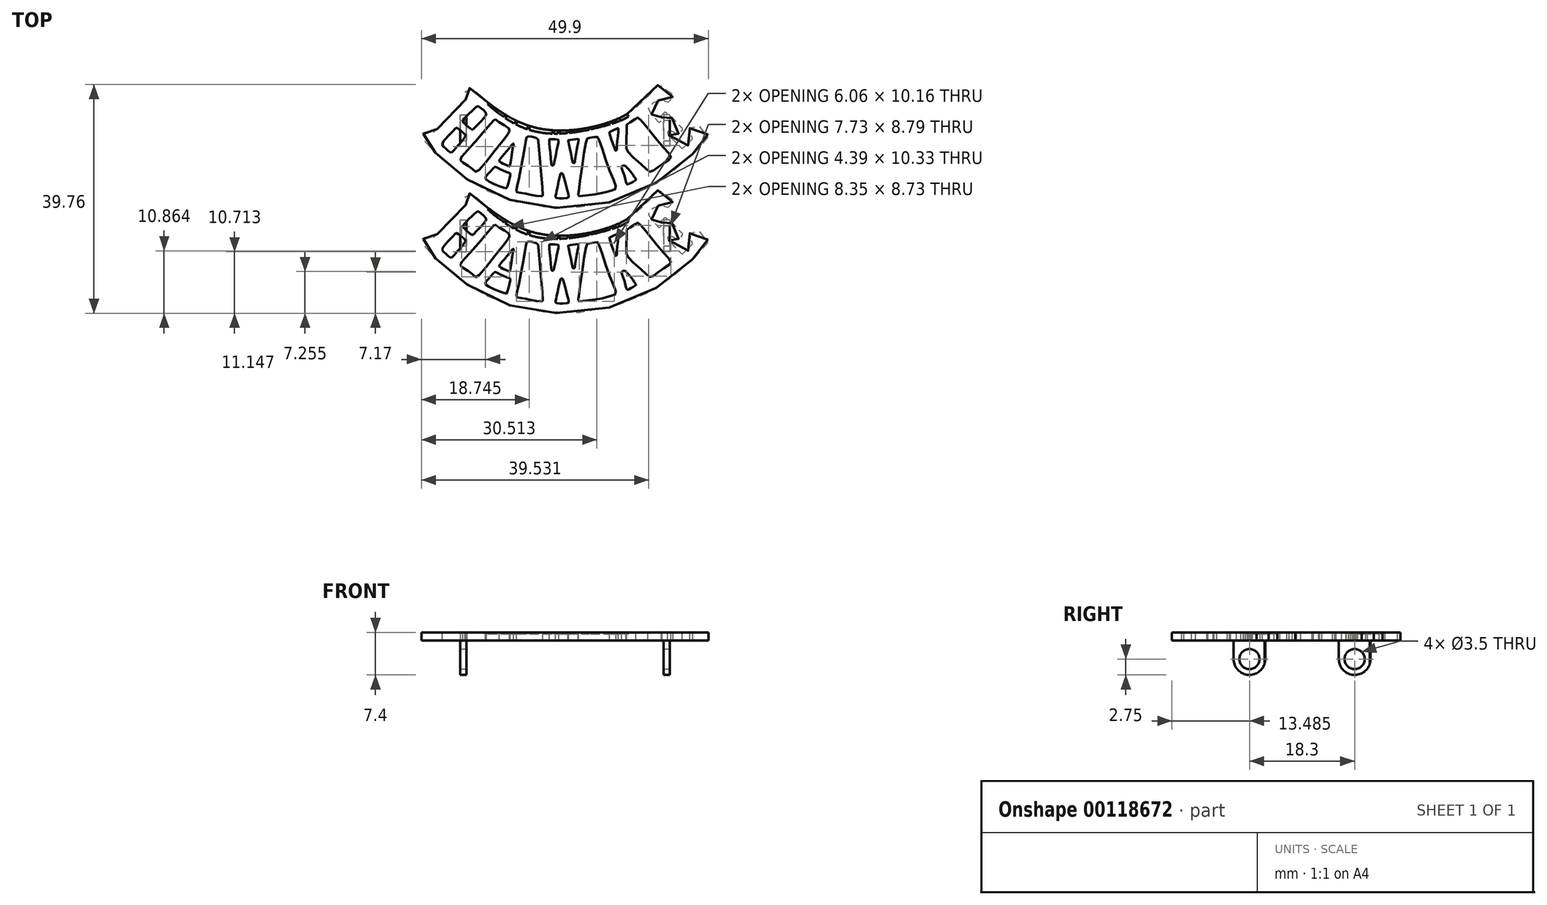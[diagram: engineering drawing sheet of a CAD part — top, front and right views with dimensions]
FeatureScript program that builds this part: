
annotation { "Feature Type Name" : "Feature", "Feature Type Description" : "" }
export const myFeature = defineFeature(function(context is Context, id is Id, definition is map)
    precondition{}
    {
        {
            var Q0;
            Q0=qCreatedBy(makeId("Top.planeOp"),FACE);
            var sketch = newSketch(context, id + "F0", { "sketchPlane" : qUnion([Q0])});
            skLineSegment(sketch, "E0.bottom", {"start": v(-25, 25) * mm, "end": v(25, 25) * mm, "construction": true});
            skLineSegment(sketch, "E0.top", {"start": v(-25, -25) * mm, "end": v(25, -25) * mm, "construction": true});
            skLineSegment(sketch, "E0.left", {"start": v(-25, 25) * mm, "end": v(-25, -25) * mm, "construction": true});
            skLineSegment(sketch, "E0.right", {"start": v(25, 25) * mm, "end": v(25, -25) * mm, "construction": true});
            skPoint(sketch, "E0.middle", {"position": v(0, 0) * mm});
            skFitSpline(sketch, "E1", {"points": [v(-16.8, 10.33) * mm, v(-16.35, 10.54) * mm, v(-16.05, 10.38) * mm, v(-14.88, 9.2) * mm, v(-8.76, 4.94) * mm, v(-1.08, 3.08) * mm, v(7.1, 4.34) * mm, v(12.96, 7.57) * mm, v(16.13, 10.99) * mm, v(16.21, 11.07) * mm, v(16.51, 10.96) * mm, v(18.78, 9.3) * mm, v(18.8, 9.14) * mm, v(18.17, 8.01) * mm, v(18.09, 7.96) * mm, v(17.29, 8.23) * mm, v(16.27, 8.34) * mm, v(14.83, 7.46) * mm, v(14.45, 6.77) * mm, v(14.56, 6.5) * mm, v(16.27, 4.54) * mm, v(16.43, 4.4) * mm, v(16.82, 4.73) * mm, v(16.87, 5.12) * mm, v(16.76, 5.72) * mm, v(16.98, 6.03) * mm, v(17.62, 6.41) * mm, v(17.81, 6.25) * mm, v(20.02, 3.85) * mm, v(20.37, 3.55) * mm, v(20.37, 3.24) * mm, v(19.66, 2.47) * mm, v(19.4, 2.47) * mm, v(18.58, 2.94) * mm, v(17.92, 2.86) * mm, v(17.84, 2.7) * mm, v(19.96, -0.01) * mm, v(20.2, -0.15) * mm, v(21.31, 0.43) * mm, v(22.2, 1.73) * mm, v(21.95, 3.02) * mm, v(21.73, 3.43) * mm, v(21.73, 3.57) * mm, v(22.7, 4.31) * mm, v(22.82, 4.31) * mm, v(24.88, 2.33) * mm, v(24.92, 2.16) * mm, v(24.78, 1.83) * mm, v(22.72, -0.54) * mm, v(18.13, -4.47) * mm, v(12.27, -7.86) * mm, v(4.07, -10.1) * mm, v(-3.83, -10.19) * mm, v(-9.9, -8.88) * mm, v(-15.88, -6.15) * mm, v(-20.81, -2.4) * mm, v(-23.4, 0.07) * mm, v(-24.87, 1.83) * mm, v(-24.93, 2.19) * mm, v(-23.94, 3.2) * mm, v(-23.72, 3.24) * mm, v(-23.04, 2.76) * mm, v(-22.86, 2.76) * mm, v(-19, 6.6) * mm, v(-17.17, 8.55) * mm, v(-17.03, 8.82) * mm, v(-17.33, 9.62) * mm, v(-17.37, 9.78) * mm, v(-16.8, 10.33) * mm]});
            skFitSpline(sketch, "E2", {"points": [v(-16.68, 6) * mm, v(-15.57, 7.06) * mm, v(-15.24, 7.28) * mm, v(-14.93, 7.23) * mm, v(-13.75, 6.16) * mm, v(-13.7, 5.9) * mm, v(-13.9, 5.53) * mm, v(-16, 3.28) * mm, v(-16.24, 3.26) * mm, v(-17.73, 4.61) * mm, v(-17.76, 4.78) * mm, v(-17.65, 5) * mm, v(-16.68, 6) * mm]});
            skFitSpline(sketch, "E3", {"points": [v(-20.35, 2.1) * mm, v(-19.34, 3.16) * mm, v(-19, 3.52) * mm, v(-18.71, 3.52) * mm, v(-17.8, 2.75) * mm, v(-17.31, 2.32) * mm, v(-17.48, 1.83) * mm, v(-18.84, 0.23) * mm, v(-19.6, -0.61) * mm, v(-20.02, -0.71) * mm, v(-20.68, -0.08) * mm, v(-21.3, 0.47) * mm, v(-21.32, 0.86) * mm, v(-20.93, 1.47) * mm, v(-20.35, 2.1) * mm]});
            skFitSpline(sketch, "E4", {"points": [v(-15.5, 1.26) * mm, v(-13.73, 3.35) * mm, v(-12.52, 4.73) * mm, v(-12.26, 4.97) * mm, v(-12.03, 4.97) * mm, v(-11.45, 4.49) * mm, v(-9.9, 3.58) * mm, v(-9.66, 3.22) * mm, v(-9.68, 2.82) * mm, v(-11, 1.11) * mm, v(-15.2, -4.01) * mm, v(-15.59, -4.08) * mm, v(-16.2, -3.51) * mm, v(-17.4, -2.7) * mm, v(-18.1, -2.16) * mm, v(-18.16, -1.8) * mm, v(-17.52, -0.95) * mm, v(-15.5, 1.26) * mm]});
            skFitSpline(sketch, "E5", {"points": [v(-9.17, 0.7) * mm, v(-10.6, -1.03) * mm, v(-11.39, -2) * mm, v(-11.44, -2.23) * mm, v(-10.8, -2.67) * mm, v(-9.64, -3.14) * mm, v(-9.58, -3.08) * mm, v(-8.98, 0.65) * mm, v(-8.98, 0.79) * mm, v(-9.07, 0.82) * mm, v(-9.17, 0.7) * mm]});
            skFitSpline(sketch, "E6", {"points": [v(-9.72, -4.26) * mm, v(-11.01, -3.78) * mm, v(-11.97, -3.26) * mm, v(-12.14, -3.2) * mm, v(-12.44, -3.43) * mm, v(-13.75, -4.9) * mm, v(-13.84, -5.15) * mm, v(-13.66, -5.52) * mm, v(-10.5, -6.91) * mm, v(-10.19, -6.91) * mm, v(-9.63, -5.15) * mm, v(-9.56, -4.37) * mm, v(-9.72, -4.26) * mm]});
            skFitSpline(sketch, "E7", {"points": [v(-6.8, 1.44) * mm, v(-7.66, -3.4) * mm, v(-8.38, -6.96) * mm, v(-8.47, -7.39) * mm, v(-8.4, -7.62) * mm, v(-7.21, -7.83) * mm, v(-6.26, -8.05) * mm, v(-4.53, -8.3) * mm, v(-3.88, -8.28) * mm, v(-3.84, -8.12) * mm, v(-4.62, 1.33) * mm, v(-4.67, 1.53) * mm, v(-4.86, 1.7) * mm, v(-5.45, 1.95) * mm, v(-6.28, 2.07) * mm, v(-6.59, 2.04) * mm, v(-6.72, 1.86) * mm, v(-6.8, 1.44) * mm]});
            skFitSpline(sketch, "E8", {"points": [v(-2.74, 1.4) * mm, v(-2.37, -2.7) * mm, v(-2.28, -3) * mm, v(-2.09, -2.96) * mm, v(-1.86, -2.38) * mm, v(-1.13, 1.18) * mm, v(-1.1, 1.34) * mm, v(-1.14, 1.46) * mm, v(-2.47, 1.58) * mm, v(-2.71, 1.55) * mm, v(-2.74, 1.4) * mm]});
            skFitSpline(sketch, "E9", {"points": [v(-0.83, -4.61) * mm, v(-1.37, -7.05) * mm, v(-1.61, -8.24) * mm, v(-1.61, -8.52) * mm, v(-1.1, -8.7) * mm, v(0.5, -8.6) * mm, v(0.63, -8.47) * mm, v(0.46, -7.55) * mm, v(-0.22, -5) * mm, v(-0.36, -4.54) * mm, v(-0.54, -4.3) * mm, v(-0.73, -4.41) * mm, v(-0.83, -4.61) * mm]});
            skFitSpline(sketch, "E10", {"points": [v(1.29, -2.14) * mm, v(0.68, 0.68) * mm, v(0.56, 1.17) * mm, v(0.56, 1.36) * mm, v(1.58, 1.57) * mm, v(2.32, 1.6) * mm, v(2.37, 1.4) * mm, v(2.1, 0.14) * mm, v(1.67, -2.45) * mm, v(1.6, -2.6) * mm, v(1.42, -2.54) * mm, v(1.29, -2.14) * mm]});
            skFitSpline(sketch, "E11", {"points": [v(2.51, -8.3) * mm, v(5.22, -8.01) * mm, v(7.06, -7.63) * mm, v(7.76, -7.4) * mm, v(8.66, -7.17) * mm, v(8.89, -6.8) * mm, v(8.15, -4.84) * mm, v(6.27, 0.5) * mm, v(5.7, 1.95) * mm, v(5.57, 2.01) * mm, v(4.71, 1.85) * mm, v(4.1, 1.79) * mm, v(3.9, 1.69) * mm, v(3.47, 0.18) * mm, v(2.41, -7.2) * mm, v(2.32, -8.05) * mm, v(2.38, -8.26) * mm, v(2.51, -8.3) * mm]});
            skFitSpline(sketch, "E12", {"points": [v(7.76, 2.6) * mm, v(8.68, -0.22) * mm, v(8.75, -0.38) * mm, v(8.92, -0.38) * mm, v(9, -0.1) * mm, v(9.3, 3.3) * mm, v(9.3, 3.43) * mm, v(9.26, 3.5) * mm, v(8.96, 3.37) * mm, v(7.81, 2.82) * mm, v(7.74, 2.76) * mm, v(7.76, 2.6) * mm]});
            skFitSpline(sketch, "E13", {"points": [v(10.62, -5.84) * mm, v(10, -3.8) * mm, v(9.89, -3.15) * mm, v(10.27, -3) * mm, v(10.62, -3.18) * mm, v(11.84, -4.65) * mm, v(12.34, -5.41) * mm, v(12.31, -5.5) * mm, v(11.62, -5.94) * mm, v(10.98, -6.27) * mm, v(10.86, -6.29) * mm, v(10.7, -6.13) * mm, v(10.62, -5.84) * mm]});
            skFitSpline(sketch, "E14", {"points": [v(15.97, 1.48) * mm, v(14.22, 3.68) * mm, v(12.96, 5.15) * mm, v(12.72, 5.33) * mm, v(12.5, 5.3) * mm, v(12.07, 5) * mm, v(11.03, 4.33) * mm, v(10.77, 4.13) * mm, v(10.74, 3.56) * mm, v(10.63, 0.28) * mm, v(10.74, -0.33) * mm, v(11.56, -1.27) * mm, v(13.9, -3.38) * mm, v(14.58, -4.03) * mm, v(15.04, -4.07) * mm, v(15.58, -3.75) * mm, v(16.46, -3.05) * mm, v(17.98, -2.05) * mm, v(18.33, -1.78) * mm, v(18.42, -1.4) * mm, v(17.88, -0.67) * mm, v(15.97, 1.48) * mm]});
            skSolve(sketch);
        }
        {
            var Q0;
            Q0=makeQuery(id+"F0.imprint","IMPRINT",FACE,{"disambiguationData":[TD([[makeQuery(id+"F0.imprint","IMPRINT",EDGE,{"derivedFrom":sQuery(id+"F0.wireOp",EDGE,"E1")}),-1.0]])]});
            extrude(context, id + "F1", {"entities" : qUnion([Q0]), "oppositeDirection" : true, "depth" : 1.4 * mm, "offsetDistance" : 25 * mm});
        }
        {
            var Q0;
            Q0=makeQuery(id+"F1.opExtrude","CAP_FACE",FACE,{"disambiguationData":[OSD([sQuery(id+"F0.wireOp",EDGE,"E1"),sQuery(id+"F0.wireOp",EDGE,"E2"),sQuery(id+"F0.wireOp",EDGE,"E3"),sQuery(id+"F0.wireOp",EDGE,"E4"),sQuery(id+"F0.wireOp",EDGE,"E5"),sQuery(id+"F0.wireOp",EDGE,"E6"),sQuery(id+"F0.wireOp",EDGE,"E7"),sQuery(id+"F0.wireOp",EDGE,"E8"),sQuery(id+"F0.wireOp",EDGE,"E9"),sQuery(id+"F0.wireOp",EDGE,"E10"),sQuery(id+"F0.wireOp",EDGE,"E11"),sQuery(id+"F0.wireOp",EDGE,"E12"),sQuery(id+"F0.wireOp",EDGE,"E13"),sQuery(id+"F0.wireOp",EDGE,"E14")])],"isStart":true});
            var sketch = newSketch(context, id + "F2", { "sketchPlane" : qUnion([Q0])});
            skFitSpline(sketch, "E15.0.0", {"points": [v(-16.8, 10.33) * mm, v(-17.02, 10.15) * mm, v(-17.45, 9.79) * mm, v(-17.32, 9.63) * mm, v(-16.93, 8.79) * mm, v(-17.24, 8.49) * mm, v(-18.92, 6.66) * mm, v(-22.8, 2.67) * mm, v(-23.03, 2.73) * mm, v(-23.74, 3.3) * mm, v(-23.94, 3.24) * mm, v(-25.09, 2.2) * mm, v(-24.87, 1.77) * mm, v(-23.26, -0.17) * mm, v(-20.78, -2.48) * mm, v(-15.96, -6.48) * mm, v(-9.93, -9.08) * mm, v(-3.8, -10.44) * mm, v(4.14, -10.5) * mm, v(12.37, -8.2) * mm, v(18.13, -4.69) * mm, v(22.52, -0.88) * mm, v(24.8, 1.68) * mm, v(24.92, 2.16) * mm, v(24.98, 2.36) * mm, v(22.8, 4.38) * mm, v(22.74, 4.33) * mm, v(21.63, 3.6) * mm, v(21.73, 3.42) * mm, v(22, 3) * mm, v(22.44, 1.63) * mm, v(21.46, 0.38) * mm, v(20.17, -0.22) * mm, v(19.98, -0.06) * mm, v(17.62, 2.67) * mm, v(17.93, 2.88) * mm, v(18.62, 3.1) * mm, v(19.4, 2.43) * mm, v(19.67, 2.4) * mm, v(20.47, 3.2) * mm, v(20.4, 3.6) * mm, v(19.97, 3.77) * mm, v(17.78, 6.2) * mm, v(17.66, 6.51) * mm, v(16.95, 6.02) * mm, v(16.68, 5.76) * mm, v(16.9, 5.1) * mm, v(16.9, 4.73) * mm, v(16.4, 4.32) * mm, v(16.29, 4.58) * mm, v(14.5, 6.5) * mm, v(14.4, 6.76) * mm, v(14.77, 7.59) * mm, v(16.26, 8.53) * mm, v(17.2, 8.28) * mm, v(18.1, 7.92) * mm, v(18.17, 8) * mm, v(18.84, 9.17) * mm, v(18.85, 9.31) * mm, v(16.56, 11.01) * mm, v(16.2, 11.1) * mm, v(16.08, 10.92) * mm, v(12.74, 6.78) * mm, v(7.26, 4) * mm, v(-1.2, 2.55) * mm, v(-8.68, 4.24) * mm, v(-14.76, 8.91) * mm, v(-15.97, 10.34) * mm, v(-16.36, 10.62) * mm, v(-16.61, 10.46) * mm, v(-16.8, 10.33) * mm]});
            skLineSegment(sketch, "E16", {"start": v(-13.15, 8.37) * mm, "end": v(-15.03, 6.44) * mm});
            skLineSegment(sketch, "E17.0", {"start": v(-13.04, 8.06) * mm, "end": v(-14.91, 6.13) * mm});
            skLineSegment(sketch, "E18", {"start": v(-22.3, -1.53) * mm, "end": v(-20.26, 0.58) * mm});
            skLineSegment(sketch, "E19.0", {"start": v(-22.03, -1.69) * mm, "end": v(-20, 0.42) * mm});
            skLineSegment(sketch, "E20", {"start": v(-9.91, 6.24) * mm, "end": v(-11.97, 3.94) * mm});
            skLineSegment(sketch, "E21.0", {"start": v(-9.69, 6.04) * mm, "end": v(-11.74, 3.74) * mm});
            skLineSegment(sketch, "E22", {"start": v(-19.08, -4.59) * mm, "end": v(-16.6, -1.7) * mm});
            skLineSegment(sketch, "E23.0", {"start": v(-18.85, -4.78) * mm, "end": v(-16.37, -1.89) * mm});
            skLineSegment(sketch, "E24", {"start": v(-18.02, -5.51) * mm, "end": v(-15.7, -2.48) * mm});
            skLineSegment(sketch, "E25.0", {"start": v(-17.78, -5.7) * mm, "end": v(-15.47, -2.66) * mm});
            skLineSegment(sketch, "E26", {"start": v(-7.68, 5.41) * mm, "end": v(-10, 2.31) * mm});
            skLineSegment(sketch, "E27.0", {"start": v(-7.92, 5.59) * mm, "end": v(-10.23, 2.5) * mm});
            skLineSegment(sketch, "E28", {"start": v(-6.28, 4.78) * mm, "end": v(-6.73, 1.82) * mm});
            skLineSegment(sketch, "E29.0", {"start": v(-5.98, 4.73) * mm, "end": v(-6.43, 1.78) * mm});
            skLineSegment(sketch, "E30", {"start": v(-13.98, -7.8) * mm, "end": v(-12.3, -4.8) * mm});
            skLineSegment(sketch, "E31.0", {"start": v(-13.72, -7.94) * mm, "end": v(-12.03, -4.94) * mm});
            skLineSegment(sketch, "E32", {"start": v(-12.2, -8.68) * mm, "end": v(-11, -5.3) * mm});
            skLineSegment(sketch, "E33.0", {"start": v(-11.91, -8.78) * mm, "end": v(-10.71, -5.4) * mm});
            skLineSegment(sketch, "E34", {"start": v(-7.84, -10.15) * mm, "end": v(-6.91, -6.26) * mm});
            skLineSegment(sketch, "E35.0", {"start": v(-7.54, -10.22) * mm, "end": v(-6.62, -6.33) * mm});
            skLineSegment(sketch, "E36", {"start": v(-3.73, -10.62) * mm, "end": v(-3.9, -7.27) * mm});
            skLineSegment(sketch, "E37.0", {"start": v(-4.03, -10.64) * mm, "end": v(-4.2, -7.29) * mm});
            skLineSegment(sketch, "E38", {"start": v(-2.09, -10.82) * mm, "end": v(-1.62, -8.25) * mm});
            skLineSegment(sketch, "E39.0", {"start": v(-1.8, -10.87) * mm, "end": v(-1.32, -8.3) * mm});
            skLineSegment(sketch, "E40", {"start": v(0.92, -10.9) * mm, "end": v(0.59, -8.56) * mm});
            skLineSegment(sketch, "E41.0", {"start": v(0.62, -10.95) * mm, "end": v(0.3, -8.6) * mm});
            skLineSegment(sketch, "E42", {"start": v(2.24, -10.74) * mm, "end": v(2.36, -8.22) * mm});
            skLineSegment(sketch, "E43.0", {"start": v(2.54, -10.76) * mm, "end": v(2.66, -8.24) * mm});
            skLineSegment(sketch, "E44", {"start": v(8.3, -9.8) * mm, "end": v(7.53, -6.59) * mm});
            skLineSegment(sketch, "E45.0", {"start": v(8, -9.88) * mm, "end": v(7.24, -6.66) * mm});
            skLineSegment(sketch, "E46", {"start": v(12.01, -8.54) * mm, "end": v(10.87, -5.6) * mm});
            skLineSegment(sketch, "E47.0", {"start": v(12.3, -8.43) * mm, "end": v(11.15, -5.5) * mm});
            skLineSegment(sketch, "E48", {"start": v(13.09, -7.93) * mm, "end": v(11.76, -5.25) * mm});
            skLineSegment(sketch, "E49.0", {"start": v(12.82, -8.06) * mm, "end": v(11.5, -5.38) * mm});
            skLineSegment(sketch, "E50", {"start": v(17.28, -5.7) * mm, "end": v(14.8, -2.5) * mm});
            skLineSegment(sketch, "E51.0", {"start": v(17.52, -5.52) * mm, "end": v(15.04, -2.31) * mm});
            skLineSegment(sketch, "E52", {"start": v(18.7, -4.64) * mm, "end": v(16.52, -1.88) * mm});
            skLineSegment(sketch, "E53.0", {"start": v(18.93, -4.46) * mm, "end": v(16.75, -1.69) * mm});
            skLineSegment(sketch, "E54", {"start": v(-2.14, 4.08) * mm, "end": v(-2.27, 1.13) * mm});
            skLineSegment(sketch, "E55.0", {"start": v(-1.84, 4.1) * mm, "end": v(-1.97, 1.14) * mm});
            skLineSegment(sketch, "E56", {"start": v(-0.77, 4.01) * mm, "end": v(-1.11, 1.32) * mm});
            skLineSegment(sketch, "E57.0", {"start": v(-1.07, 4.05) * mm, "end": v(-1.4, 1.36) * mm});
            skLineSegment(sketch, "E58", {"start": v(0.3, 3.53) * mm, "end": v(0.6, 1.39) * mm});
            skLineSegment(sketch, "E59.0", {"start": v(0.6, 3.57) * mm, "end": v(0.9, 1.43) * mm});
            skLineSegment(sketch, "E60", {"start": v(3.99, 4.37) * mm, "end": v(4.78, 0.95) * mm});
            skLineSegment(sketch, "E61.0", {"start": v(4.28, 4.43) * mm, "end": v(5.07, 1.02) * mm});
            skLineSegment(sketch, "E62", {"start": v(7.4, 5.44) * mm, "end": v(8.53, 2.45) * mm});
            skLineSegment(sketch, "E63.0", {"start": v(7.68, 5.55) * mm, "end": v(8.8, 2.55) * mm});
            skLineSegment(sketch, "E64", {"start": v(10.22, 6.93) * mm, "end": v(11.97, 3.94) * mm});
            skLineSegment(sketch, "E65.0", {"start": v(10.48, 7.08) * mm, "end": v(12.23, 4.09) * mm});
            skSolve(sketch);
        }
        {
            var Q0;
            {var subQ0=sQuery(id+"F2.wireOp",EDGE,"E17.0");var subQ1=sQuery(id+"F2.wireOp",EDGE,"E15.0.0");var subQ2=makeQuery(id+"F2.imprint","INTERSECT",VERTEX,{"derivedFrom":[subQ1,subQ0]});Q0=makeQuery(id+"F2.imprint","IMPRINT",FACE,{"disambiguationData":[TD([[makeQuery(id+"F2.imprint","IMPRINT",EDGE,{"disambiguationData":[TD([[subQ2,1.0]])],"derivedFrom":subQ1}),-1.0]])]});}
            var Q1;
            {var subQ0=sQuery(id+"F2.wireOp",EDGE,"E20");var subQ1=sQuery(id+"F2.wireOp",EDGE,"E15.0.0");var subQ2=makeQuery(id+"F2.imprint","INTERSECT",VERTEX,{"derivedFrom":[subQ1,subQ0]});Q1=makeQuery(id+"F2.imprint","IMPRINT",FACE,{"disambiguationData":[TD([[makeQuery(id+"F2.imprint","IMPRINT",EDGE,{"disambiguationData":[TD([[subQ2,-1.0]])],"derivedFrom":subQ1}),-1.0]])]});}
            var Q2;
            {var subQ0=sQuery(id+"F2.wireOp",EDGE,"E27.0");var subQ1=sQuery(id+"F2.wireOp",EDGE,"E15.0.0");var subQ2=makeQuery(id+"F2.imprint","INTERSECT",VERTEX,{"derivedFrom":[subQ1,subQ0]});Q2=makeQuery(id+"F2.imprint","IMPRINT",FACE,{"disambiguationData":[TD([[makeQuery(id+"F2.imprint","IMPRINT",EDGE,{"disambiguationData":[TD([[subQ2,-1.0]])],"derivedFrom":subQ1}),-1.0]])]});}
            var Q3;
            {var subQ0=sQuery(id+"F2.wireOp",EDGE,"E28");var subQ1=sQuery(id+"F2.wireOp",EDGE,"E15.0.0");var subQ2=makeQuery(id+"F2.imprint","INTERSECT",VERTEX,{"derivedFrom":[subQ1,subQ0]});Q3=makeQuery(id+"F2.imprint","IMPRINT",FACE,{"disambiguationData":[TD([[makeQuery(id+"F2.imprint","IMPRINT",EDGE,{"disambiguationData":[TD([[subQ2,-1.0]])],"derivedFrom":subQ1}),-1.0]])]});}
            var Q4;
            {var subQ0=sQuery(id+"F2.wireOp",EDGE,"E57.0");var subQ1=sQuery(id+"F2.wireOp",EDGE,"E15.0.0");var subQ2=makeQuery(id+"F2.imprint","INTERSECT",VERTEX,{"derivedFrom":[subQ1,subQ0]});Q4=makeQuery(id+"F2.imprint","IMPRINT",FACE,{"disambiguationData":[TD([[makeQuery(id+"F2.imprint","IMPRINT",EDGE,{"disambiguationData":[TD([[subQ2,-1.0]])],"derivedFrom":subQ1}),-1.0]])]});}
            var Q5;
            {var subQ0=sQuery(id+"F2.wireOp",EDGE,"E54");var subQ1=sQuery(id+"F2.wireOp",EDGE,"E15.0.0");var subQ2=makeQuery(id+"F2.imprint","INTERSECT",VERTEX,{"derivedFrom":[subQ1,subQ0]});Q5=makeQuery(id+"F2.imprint","IMPRINT",FACE,{"disambiguationData":[TD([[makeQuery(id+"F2.imprint","IMPRINT",EDGE,{"disambiguationData":[TD([[subQ2,-1.0]])],"derivedFrom":subQ1}),-1.0]])]});}
            var Q6;
            {var subQ0=sQuery(id+"F2.wireOp",EDGE,"E58");var subQ1=sQuery(id+"F2.wireOp",EDGE,"E15.0.0");var subQ2=makeQuery(id+"F2.imprint","INTERSECT",VERTEX,{"derivedFrom":[subQ1,subQ0]});Q6=makeQuery(id+"F2.imprint","IMPRINT",FACE,{"disambiguationData":[TD([[makeQuery(id+"F2.imprint","IMPRINT",EDGE,{"disambiguationData":[TD([[subQ2,-1.0]])],"derivedFrom":subQ1}),-1.0]])]});}
            var Q7;
            {var subQ0=sQuery(id+"F2.wireOp",EDGE,"E60");var subQ1=sQuery(id+"F2.wireOp",EDGE,"E15.0.0");var subQ2=makeQuery(id+"F2.imprint","INTERSECT",VERTEX,{"derivedFrom":[subQ1,subQ0]});Q7=makeQuery(id+"F2.imprint","IMPRINT",FACE,{"disambiguationData":[TD([[makeQuery(id+"F2.imprint","IMPRINT",EDGE,{"disambiguationData":[TD([[subQ2,-1.0]])],"derivedFrom":subQ1}),-1.0]])]});}
            var Q8;
            {var subQ0=sQuery(id+"F2.wireOp",EDGE,"E62");var subQ1=sQuery(id+"F2.wireOp",EDGE,"E15.0.0");var subQ2=makeQuery(id+"F2.imprint","INTERSECT",VERTEX,{"derivedFrom":[subQ1,subQ0]});Q8=makeQuery(id+"F2.imprint","IMPRINT",FACE,{"disambiguationData":[TD([[makeQuery(id+"F2.imprint","IMPRINT",EDGE,{"disambiguationData":[TD([[subQ2,-1.0]])],"derivedFrom":subQ1}),-1.0]])]});}
            var Q9;
            {var subQ0=sQuery(id+"F2.wireOp",EDGE,"E64");var subQ1=sQuery(id+"F2.wireOp",EDGE,"E15.0.0");var subQ2=makeQuery(id+"F2.imprint","INTERSECT",VERTEX,{"derivedFrom":[subQ1,subQ0]});Q9=makeQuery(id+"F2.imprint","IMPRINT",FACE,{"disambiguationData":[TD([[makeQuery(id+"F2.imprint","IMPRINT",EDGE,{"disambiguationData":[TD([[subQ2,-1.0]])],"derivedFrom":subQ1}),-1.0]])]});}
            var Q10;
            {var subQ0=sQuery(id+"F2.wireOp",EDGE,"E19.0");var subQ1=sQuery(id+"F2.wireOp",EDGE,"E15.0.0");var subQ2=makeQuery(id+"F2.imprint","INTERSECT",VERTEX,{"derivedFrom":[subQ1,subQ0]});Q10=makeQuery(id+"F2.imprint","IMPRINT",FACE,{"disambiguationData":[TD([[makeQuery(id+"F2.imprint","IMPRINT",EDGE,{"disambiguationData":[TD([[subQ2,-1.0]])],"derivedFrom":subQ1}),-1.0]])]});}
            var Q11;
            {var subQ0=sQuery(id+"F2.wireOp",EDGE,"E23.0");var subQ1=sQuery(id+"F2.wireOp",EDGE,"E15.0.0");var subQ2=makeQuery(id+"F2.imprint","INTERSECT",VERTEX,{"derivedFrom":[subQ1,subQ0]});Q11=makeQuery(id+"F2.imprint","IMPRINT",FACE,{"disambiguationData":[TD([[makeQuery(id+"F2.imprint","IMPRINT",EDGE,{"disambiguationData":[TD([[subQ2,-1.0]])],"derivedFrom":subQ1}),-1.0]])]});}
            var Q12;
            {var subQ0=sQuery(id+"F2.wireOp",EDGE,"E25.0");var subQ1=sQuery(id+"F2.wireOp",EDGE,"E15.0.0");var subQ2=makeQuery(id+"F2.imprint","INTERSECT",VERTEX,{"derivedFrom":[subQ1,subQ0]});Q12=makeQuery(id+"F2.imprint","IMPRINT",FACE,{"disambiguationData":[TD([[makeQuery(id+"F2.imprint","IMPRINT",EDGE,{"disambiguationData":[TD([[subQ2,-1.0]])],"derivedFrom":subQ1}),-1.0]])]});}
            var Q13;
            {var subQ0=sQuery(id+"F2.wireOp",EDGE,"E31.0");var subQ1=sQuery(id+"F2.wireOp",EDGE,"E15.0.0");var subQ2=makeQuery(id+"F2.imprint","INTERSECT",VERTEX,{"derivedFrom":[subQ1,subQ0]});Q13=makeQuery(id+"F2.imprint","IMPRINT",FACE,{"disambiguationData":[TD([[makeQuery(id+"F2.imprint","IMPRINT",EDGE,{"disambiguationData":[TD([[subQ2,-1.0]])],"derivedFrom":subQ1}),-1.0]])]});}
            var Q14;
            {var subQ0=sQuery(id+"F2.wireOp",EDGE,"E33.0");var subQ1=sQuery(id+"F2.wireOp",EDGE,"E15.0.0");var subQ2=makeQuery(id+"F2.imprint","INTERSECT",VERTEX,{"derivedFrom":[subQ1,subQ0]});Q14=makeQuery(id+"F2.imprint","IMPRINT",FACE,{"disambiguationData":[TD([[makeQuery(id+"F2.imprint","IMPRINT",EDGE,{"disambiguationData":[TD([[subQ2,-1.0]])],"derivedFrom":subQ1}),-1.0]])]});}
            var Q15;
            {var subQ0=sQuery(id+"F2.wireOp",EDGE,"E35.0");var subQ1=sQuery(id+"F2.wireOp",EDGE,"E15.0.0");var subQ2=makeQuery(id+"F2.imprint","INTERSECT",VERTEX,{"derivedFrom":[subQ1,subQ0]});Q15=makeQuery(id+"F2.imprint","IMPRINT",FACE,{"disambiguationData":[TD([[makeQuery(id+"F2.imprint","IMPRINT",EDGE,{"disambiguationData":[TD([[subQ2,-1.0]])],"derivedFrom":subQ1}),-1.0]])]});}
            var Q16;
            {var subQ0=sQuery(id+"F2.wireOp",EDGE,"E36");var subQ1=sQuery(id+"F2.wireOp",EDGE,"E15.0.0");var subQ2=makeQuery(id+"F2.imprint","INTERSECT",VERTEX,{"derivedFrom":[subQ1,subQ0]});Q16=makeQuery(id+"F2.imprint","IMPRINT",FACE,{"disambiguationData":[TD([[makeQuery(id+"F2.imprint","IMPRINT",EDGE,{"disambiguationData":[TD([[subQ2,-1.0]])],"derivedFrom":subQ1}),-1.0]])]});}
            var Q17;
            {var subQ0=sQuery(id+"F2.wireOp",EDGE,"E39.0");var subQ1=sQuery(id+"F2.wireOp",EDGE,"E15.0.0");var subQ2=makeQuery(id+"F2.imprint","INTERSECT",VERTEX,{"derivedFrom":[subQ1,subQ0]});Q17=makeQuery(id+"F2.imprint","IMPRINT",FACE,{"disambiguationData":[TD([[makeQuery(id+"F2.imprint","IMPRINT",EDGE,{"disambiguationData":[TD([[subQ2,-1.0]])],"derivedFrom":subQ1}),-1.0]])]});}
            var Q18;
            {var subQ0=sQuery(id+"F2.wireOp",EDGE,"E40");var subQ1=sQuery(id+"F2.wireOp",EDGE,"E15.0.0");var subQ2=makeQuery(id+"F2.imprint","INTERSECT",VERTEX,{"derivedFrom":[subQ1,subQ0]});Q18=makeQuery(id+"F2.imprint","IMPRINT",FACE,{"disambiguationData":[TD([[makeQuery(id+"F2.imprint","IMPRINT",EDGE,{"disambiguationData":[TD([[subQ2,-1.0]])],"derivedFrom":subQ1}),-1.0]])]});}
            var Q19;
            {var subQ0=sQuery(id+"F2.wireOp",EDGE,"E43.0");var subQ1=sQuery(id+"F2.wireOp",EDGE,"E15.0.0");var subQ2=makeQuery(id+"F2.imprint","INTERSECT",VERTEX,{"derivedFrom":[subQ1,subQ0]});Q19=makeQuery(id+"F2.imprint","IMPRINT",FACE,{"disambiguationData":[TD([[makeQuery(id+"F2.imprint","IMPRINT",EDGE,{"disambiguationData":[TD([[subQ2,-1.0]])],"derivedFrom":subQ1}),-1.0]])]});}
            var Q20;
            {var subQ0=sQuery(id+"F2.wireOp",EDGE,"E44");var subQ1=sQuery(id+"F2.wireOp",EDGE,"E15.0.0");var subQ2=makeQuery(id+"F2.imprint","INTERSECT",VERTEX,{"derivedFrom":[subQ1,subQ0]});Q20=makeQuery(id+"F2.imprint","IMPRINT",FACE,{"disambiguationData":[TD([[makeQuery(id+"F2.imprint","IMPRINT",EDGE,{"disambiguationData":[TD([[subQ2,-1.0]])],"derivedFrom":subQ1}),-1.0]])]});}
            var Q21;
            {var subQ0=sQuery(id+"F2.wireOp",EDGE,"E47.0");var subQ1=sQuery(id+"F2.wireOp",EDGE,"E15.0.0");var subQ2=makeQuery(id+"F2.imprint","INTERSECT",VERTEX,{"derivedFrom":[subQ1,subQ0]});Q21=makeQuery(id+"F2.imprint","IMPRINT",FACE,{"disambiguationData":[TD([[makeQuery(id+"F2.imprint","IMPRINT",EDGE,{"disambiguationData":[TD([[subQ2,-1.0]])],"derivedFrom":subQ1}),-1.0]])]});}
            var Q22;
            {var subQ0=sQuery(id+"F2.wireOp",EDGE,"E48");var subQ1=sQuery(id+"F2.wireOp",EDGE,"E15.0.0");var subQ2=makeQuery(id+"F2.imprint","INTERSECT",VERTEX,{"derivedFrom":[subQ1,subQ0]});Q22=makeQuery(id+"F2.imprint","IMPRINT",FACE,{"disambiguationData":[TD([[makeQuery(id+"F2.imprint","IMPRINT",EDGE,{"disambiguationData":[TD([[subQ2,-1.0]])],"derivedFrom":subQ1}),-1.0]])]});}
            var Q23;
            {var subQ0=sQuery(id+"F2.wireOp",EDGE,"E51.0");var subQ1=sQuery(id+"F2.wireOp",EDGE,"E15.0.0");var subQ2=makeQuery(id+"F2.imprint","INTERSECT",VERTEX,{"derivedFrom":[subQ1,subQ0]});Q23=makeQuery(id+"F2.imprint","IMPRINT",FACE,{"disambiguationData":[TD([[makeQuery(id+"F2.imprint","IMPRINT",EDGE,{"disambiguationData":[TD([[subQ2,-1.0]])],"derivedFrom":subQ1}),-1.0]])]});}
            var Q24;
            {var subQ0=sQuery(id+"F2.wireOp",EDGE,"E53.0");var subQ1=sQuery(id+"F2.wireOp",EDGE,"E15.0.0");var subQ2=makeQuery(id+"F2.imprint","INTERSECT",VERTEX,{"derivedFrom":[subQ1,subQ0]});Q24=makeQuery(id+"F2.imprint","IMPRINT",FACE,{"disambiguationData":[TD([[makeQuery(id+"F2.imprint","IMPRINT",EDGE,{"disambiguationData":[TD([[subQ2,-1.0]])],"derivedFrom":subQ1}),-1.0]])]});}
            extrude(context, id + "F3", {"entities" : qUnion([Q0, Q1, Q2, Q3, Q4, Q5, Q6, Q7, Q8, Q9, Q10, Q11, Q12, Q13, Q14, Q15, Q16, Q17, Q18, Q19, Q20, Q21, Q22, Q23, Q24]), "operationType" : NewBodyOperationType.REMOVE, "oppositeDirection" : true, "depth" : 0.3 * mm, "offsetDistance" : 25 * mm});
        }
        {
            var Q0;
            Q0=makeQuery(id+"F1.opExtrude","CAP_FACE",FACE,{"disambiguationData":[OSD([sQuery(id+"F0.wireOp",EDGE,"E1"),sQuery(id+"F0.wireOp",EDGE,"E2"),sQuery(id+"F0.wireOp",EDGE,"E3"),sQuery(id+"F0.wireOp",EDGE,"E4"),sQuery(id+"F0.wireOp",EDGE,"E5"),sQuery(id+"F0.wireOp",EDGE,"E6"),sQuery(id+"F0.wireOp",EDGE,"E7"),sQuery(id+"F0.wireOp",EDGE,"E8"),sQuery(id+"F0.wireOp",EDGE,"E9"),sQuery(id+"F0.wireOp",EDGE,"E10"),sQuery(id+"F0.wireOp",EDGE,"E11"),sQuery(id+"F0.wireOp",EDGE,"E12"),sQuery(id+"F0.wireOp",EDGE,"E13"),sQuery(id+"F0.wireOp",EDGE,"E14")])],"isStart":false});
            var sketch = newSketch(context, id + "F4", { "sketchPlane" : qUnion([Q0])});
            skLineSegment(sketch, "E66.bottom", {"start": v(18.25, -5.84) * mm, "end": v(-18.25, -5.84) * mm, "construction": true});
            skLineSegment(sketch, "E66.top", {"start": v(18.25, -0.34) * mm, "end": v(-18.25, -0.34) * mm, "construction": true});
            skLineSegment(sketch, "E66.left", {"start": v(18.25, -5.84) * mm, "end": v(18.25, -0.34) * mm, "construction": true});
            skLineSegment(sketch, "E66.right", {"start": v(-18.25, -5.84) * mm, "end": v(-18.25, -0.34) * mm, "construction": true});
            skPoint(sketch, "E66.middle", {"position": v(0, -3.1) * mm});
            skLineSegment(sketch, "E67.bottom", {"start": v(18.25, -5.84) * mm, "end": v(17.15, -5.84) * mm});
            skLineSegment(sketch, "E67.top", {"start": v(18.25, -0.34) * mm, "end": v(17.15, -0.34) * mm});
            skLineSegment(sketch, "E67.left", {"start": v(18.25, -5.84) * mm, "end": v(18.25, -0.34) * mm});
            skLineSegment(sketch, "E67.right", {"start": v(17.15, -5.84) * mm, "end": v(17.15, -0.34) * mm});
            skLineSegment(sketch, "E68.bottom", {"start": v(-18.25, -0.34) * mm, "end": v(-17.15, -0.34) * mm});
            skLineSegment(sketch, "E68.top", {"start": v(-18.25, -5.84) * mm, "end": v(-17.15, -5.84) * mm});
            skLineSegment(sketch, "E68.left", {"start": v(-18.25, -0.34) * mm, "end": v(-18.25, -5.84) * mm});
            skLineSegment(sketch, "E68.right", {"start": v(-17.15, -0.34) * mm, "end": v(-17.15, -5.84) * mm});
            skSolve(sketch);
        }
        {
            var Q0;
            {var subQ0=sQuery(id+"F4.wireOp",EDGE,"E67.left");var subQ1=makeQuery(id+"F1.opExtrude","CAP_EDGE",EDGE,{"disambiguationData":[OSD([sQuery(id+"F0.wireOp",EDGE,"E14")])],"isStart":false});var subQ2=makeQuery(id+"F4.imprint","INTERSECT",VERTEX,{"disambiguationData":[OD(0.0)],"derivedFrom":[subQ1,subQ0]});Q0=makeQuery(id+"F4.imprint","IMPRINT",FACE,{"disambiguationData":[TD([[makeQuery(id+"F4.imprint","IMPRINT",EDGE,{"disambiguationData":[TD([[subQ2,-1.0]])],"derivedFrom":subQ0}),1.0]])]});}
            var Q1;
            {var subQ0=sQuery(id+"F4.wireOp",EDGE,"E67.bottom");Q1=makeQuery(id+"F4.imprint","IMPRINT",FACE,{"disambiguationData":[TD([[makeQuery(id+"F4.imprint","IMPRINT",EDGE,{"derivedFrom":subQ0}),-1.0]])]});}
            var Q2;
            {var subQ0=sQuery(id+"F4.wireOp",EDGE,"E67.top");Q2=makeQuery(id+"F4.imprint","IMPRINT",FACE,{"disambiguationData":[TD([[makeQuery(id+"F4.imprint","IMPRINT",EDGE,{"derivedFrom":subQ0}),1.0]])]});}
            var Q3;
            {var subQ1=sQuery(id+"F4.wireOp",EDGE,"E68.bottom");Q3=makeQuery(id+"F4.imprint","IMPRINT",FACE,{"disambiguationData":[TD([[makeQuery(id+"F4.imprint","IMPRINT",EDGE,{"derivedFrom":subQ1}),-1.0]])]});}
            var Q4;
            {var subQ0=sQuery(id+"F4.wireOp",EDGE,"E68.right");var subQ1=makeQuery(id+"F1.opExtrude","CAP_EDGE",EDGE,{"disambiguationData":[OSD([sQuery(id+"F0.wireOp",EDGE,"E4")])],"isStart":false});var subQ2=makeQuery(id+"F4.imprint","INTERSECT",VERTEX,{"disambiguationData":[OD(0.0)],"derivedFrom":[subQ1,subQ0]});Q4=makeQuery(id+"F4.imprint","IMPRINT",FACE,{"disambiguationData":[TD([[makeQuery(id+"F4.imprint","IMPRINT",EDGE,{"disambiguationData":[TD([[subQ2,-1.0]])],"derivedFrom":subQ0}),-1.0]])]});}
            var Q5;
            {var subQ0=sQuery(id+"F4.wireOp",EDGE,"E68.left");var subQ1=sQuery(id+"F4.wireOp",EDGE,"E68.top");var subQ2=makeQuery(id+"F4.imprint","INTERSECT",VERTEX,{"derivedFrom":[subQ1,subQ0]});Q5=makeQuery(id+"F4.imprint","IMPRINT",FACE,{"disambiguationData":[TD([[makeQuery(id+"F4.imprint","IMPRINT",EDGE,{"disambiguationData":[TD([[subQ2,-1.0]])],"derivedFrom":subQ1}),1.0]])]});}
            var Q6;
            {var subQ0=sQuery(id+"F4.wireOp",EDGE,"E68.left");var subQ1=makeQuery(id+"F1.opExtrude","CAP_EDGE",EDGE,{"disambiguationData":[OSD([sQuery(id+"F0.wireOp",EDGE,"E3")])],"isStart":false});var subQ2=makeQuery(id+"F4.imprint","INTERSECT",VERTEX,{"disambiguationData":[OD(0.0)],"derivedFrom":[subQ1,subQ0]});Q6=makeQuery(id+"F4.imprint","IMPRINT",FACE,{"disambiguationData":[TD([[makeQuery(id+"F4.imprint","IMPRINT",EDGE,{"disambiguationData":[TD([[subQ2,-1.0]])],"derivedFrom":subQ0}),1.0]])]});}
            var Q7;
            {var subQ0=sQuery(id+"F4.wireOp",EDGE,"E67.left");var subQ1=makeQuery(id+"F1.opExtrude","CAP_EDGE",EDGE,{"disambiguationData":[OSD([sQuery(id+"F0.wireOp",EDGE,"E1")])],"isStart":false});var subQ2=makeQuery(id+"F4.imprint","INTERSECT",VERTEX,{"disambiguationData":[OD(1.0)],"derivedFrom":[subQ1,subQ0]});Q7=makeQuery(id+"F4.imprint","IMPRINT",FACE,{"disambiguationData":[TD([[makeQuery(id+"F4.imprint","IMPRINT",EDGE,{"disambiguationData":[TD([[subQ2,-1.0]])],"derivedFrom":subQ0}),1.0]])]});}
            extrude(context, id + "F5", {"entities" : qUnion([Q0, Q1, Q2, Q3, Q4, Q5, Q6, Q7]), "operationType" : NewBodyOperationType.ADD, "depth" : 6 * mm, "offsetDistance" : 25 * mm});
        }
        {
            var Q0;
            Q0=makeQuery(id+"F5.opExtrude","CAP_EDGE",EDGE,{"disambiguationData":[OSD([sQuery(id+"F4.wireOp",EDGE,"E68.top")])],"isStart":false});
            var Q1;
            Q1=makeQuery(id+"F5.opExtrude","CAP_EDGE",EDGE,{"disambiguationData":[OSD([sQuery(id+"F4.wireOp",EDGE,"E68.bottom")])],"isStart":false});
            var Q2;
            Q2=makeQuery(id+"F5.opExtrude","CAP_EDGE",EDGE,{"disambiguationData":[OSD([sQuery(id+"F4.wireOp",EDGE,"E67.bottom")])],"isStart":false});
            var Q3;
            Q3=makeQuery(id+"F5.opExtrude","CAP_EDGE",EDGE,{"disambiguationData":[OSD([sQuery(id+"F4.wireOp",EDGE,"E67.top")])],"isStart":false});
            fillet(context, id + "F6", {"entities" : qUnion([Q0, Q1, Q2, Q3]), "tangentPropagation" : true, "radius" : 2.75 * mm, "defaultsChanged" : true, "vertexSettings" : [], "allowEdgeOverflow" : false});
        }
        {
            var Q0;
            {var subQ0=sQuery(id+"F0.wireOp",EDGE,"E1");var subQ1=sQuery(id+"F4.wireOp",EDGE,"E67.bottom");var subQ2=sQuery(id+"F4.wireOp",EDGE,"E67.left");Q0=makeQuery(id+"F5.boolean.opBoolean","SPLIT",FACE,{"disambiguationData":[TD([makeQuery(id+"F1.opExtrude","SWEPT_FACE",FACE,{"disambiguationData":[OSD([subQ0])]}),makeQuery(id+"F1.opExtrude","CAP_FACE",FACE,{"disambiguationData":[OSD([subQ0,sQuery(id+"F0.wireOp",EDGE,"E2"),sQuery(id+"F0.wireOp",EDGE,"E3"),sQuery(id+"F0.wireOp",EDGE,"E4"),sQuery(id+"F0.wireOp",EDGE,"E5"),sQuery(id+"F0.wireOp",EDGE,"E6"),sQuery(id+"F0.wireOp",EDGE,"E7"),sQuery(id+"F0.wireOp",EDGE,"E8"),sQuery(id+"F0.wireOp",EDGE,"E9"),sQuery(id+"F0.wireOp",EDGE,"E10"),sQuery(id+"F0.wireOp",EDGE,"E11"),sQuery(id+"F0.wireOp",EDGE,"E12"),sQuery(id+"F0.wireOp",EDGE,"E13"),sQuery(id+"F0.wireOp",EDGE,"E14")])],"isStart":false}),makeQuery(id+"F5.opExtrude","SWEPT_FACE",FACE,{"disambiguationData":[OSD([subQ1])]}),makeQuery(id+"F5.opExtrude","SWEPT_FACE",FACE,{"disambiguationData":[OSD([subQ2])]})])],"derivedFrom":makeQuery(id+"F5.opExtrude","CAP_FACE",FACE,{"disambiguationData":[OSD([subQ1,sQuery(id+"F4.wireOp",EDGE,"E67.top"),subQ2,sQuery(id+"F4.wireOp",EDGE,"E67.right")])],"isStart":true})});}
            extrude(context, id + "F7", {"entities" : qUnion([Q0]), "operationType" : NewBodyOperationType.REMOVE, "oppositeDirection" : true, "depth" : 25 * mm, "offsetDistance" : 25 * mm});
        }
        {
            var Q0;
            Q0=makeQuery(id+"F5.opExtrude","SWEPT_FACE",FACE,{"disambiguationData":[OSD([sQuery(id+"F4.wireOp",EDGE,"E67.left")])]});
            var sketch = newSketch(context, id + "F8", { "sketchPlane" : qUnion([Q0])});
            skCircle(sketch, "E69", {"center": v(3.1, -4.65) * mm, "radius": 1.75 * mm});
            skSolve(sketch);
        }
        {
            var Q0;
            Q0=makeQuery(id+"F8.imprint","IMPRINT",FACE,{"disambiguationData":[TD([[makeQuery(id+"F8.imprint","IMPRINT",EDGE,{"derivedFrom":sQuery(id+"F8.wireOp",EDGE,"E69")}),1.0]])]});
            extrude(context, id + "F9", {"entities" : qUnion([Q0]), "operationType" : NewBodyOperationType.REMOVE, "endBound" : BoundingType.THROUGH_ALL, "oppositeDirection" : true, "depth" : 25 * mm, "offsetDistance" : 25 * mm});
        }
        {
            var Q0;
            Q0=makeQuery(id+"F1.opExtrude","SWEPT_BODY",BODY,{"disambiguationData":[OSD([sQuery(id+"F0.wireOp",EDGE,"E1"),sQuery(id+"F0.wireOp",EDGE,"E2"),sQuery(id+"F0.wireOp",EDGE,"E3"),sQuery(id+"F0.wireOp",EDGE,"E4"),sQuery(id+"F0.wireOp",EDGE,"E5"),sQuery(id+"F0.wireOp",EDGE,"E6"),sQuery(id+"F0.wireOp",EDGE,"E7"),sQuery(id+"F0.wireOp",EDGE,"E8"),sQuery(id+"F0.wireOp",EDGE,"E9"),sQuery(id+"F0.wireOp",EDGE,"E10"),sQuery(id+"F0.wireOp",EDGE,"E11"),sQuery(id+"F0.wireOp",EDGE,"E12"),sQuery(id+"F0.wireOp",EDGE,"E13"),sQuery(id+"F0.wireOp",EDGE,"E14")])]});
            transform(context, id + "F10", {"entities" : qUnion([Q0]), "transformType" : TransformType.TRANSLATION_3D, "dx" : 0 * mm, "dy" : 18.3 * mm, "dz" : 0 * mm, "makeCopy" : true});
        }
    });
